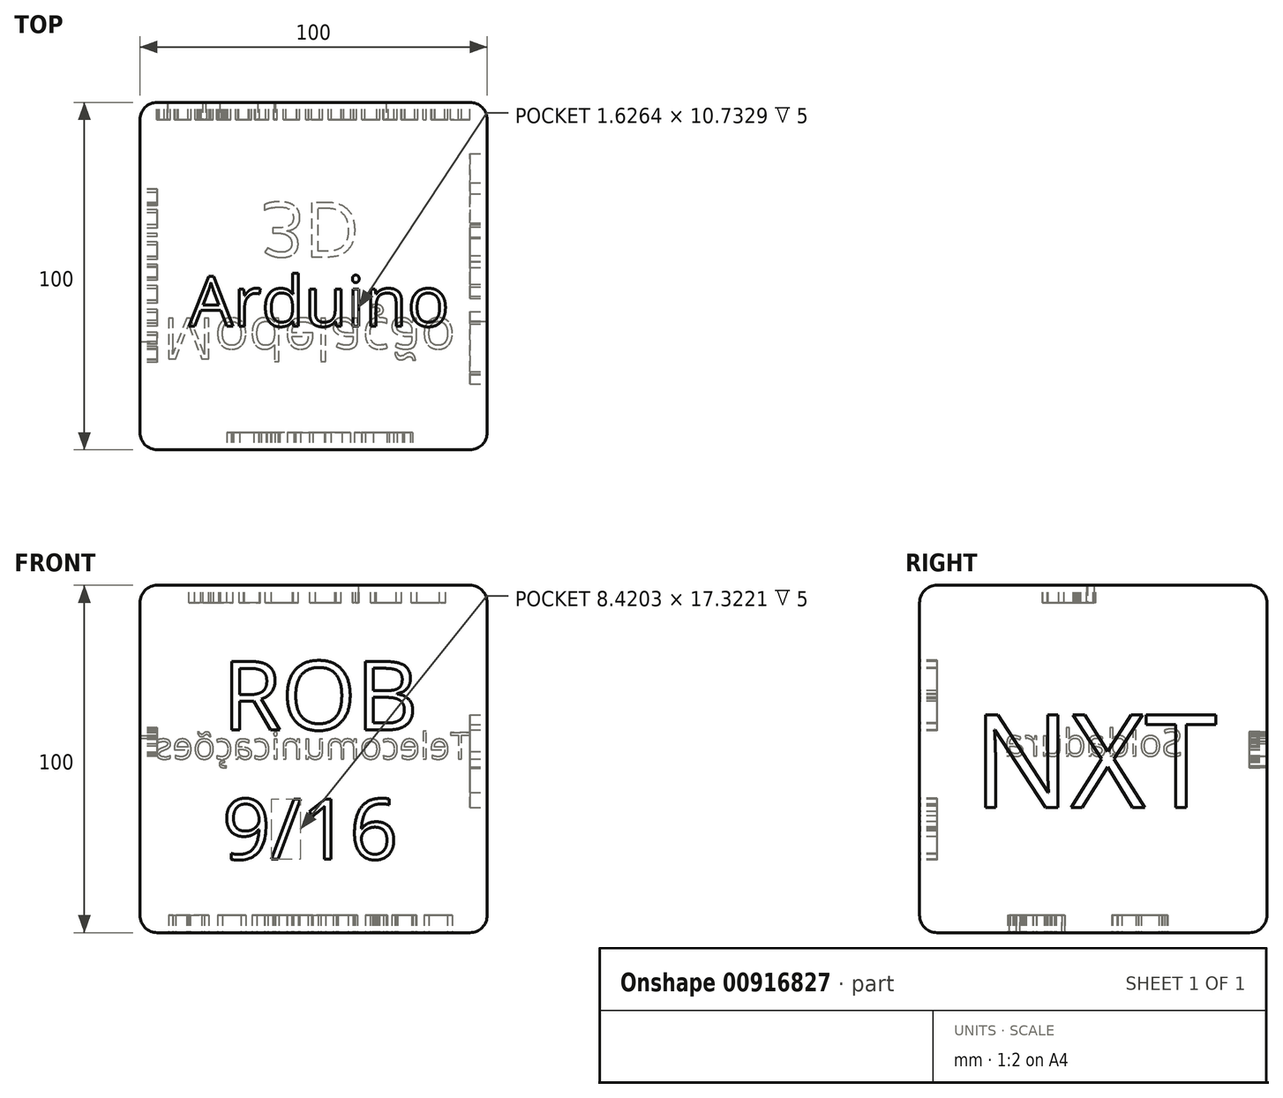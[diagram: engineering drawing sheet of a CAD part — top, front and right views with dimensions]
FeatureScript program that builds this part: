
annotation { "Feature Type Name" : "Feature", "Feature Type Description" : "" }
export const myFeature = defineFeature(function(context is Context, id is Id, definition is map)
    precondition{}
    {
        {
            var Q0;
            Q0=qCreatedBy(makeId("Top.planeOp"),FACE);
            var sketch = newSketch(context, id + "F0", { "sketchPlane" : qUnion([Q0])});
            skLineSegment(sketch, "E0.bottom", {"start": v(50, -50) * mm, "end": v(-50, -50) * mm});
            skLineSegment(sketch, "E0.top", {"start": v(50, 50) * mm, "end": v(-50, 50) * mm});
            skLineSegment(sketch, "E0.left", {"start": v(50, -50) * mm, "end": v(50, 50) * mm});
            skLineSegment(sketch, "E0.right", {"start": v(-50, -50) * mm, "end": v(-50, 50) * mm});
            skPoint(sketch, "E0.middle", {"position": v(0, 0) * mm});
            skSolve(sketch);
        }
        {
            var Q0;
            Q0=makeQuery(id+"F0.imprint","IMPRINT",FACE,{"disambiguationData":[TD([[makeQuery(id+"F0.imprint","IMPRINT",EDGE,{"derivedFrom":sQuery(id+"F0.wireOp",EDGE,"E0.bottom")}),-1.0]])]});
            extrude(context, id + "F1", {"entities" : qUnion([Q0]), "depth" : 100 * mm, "offsetDistance" : 25 * mm});
        }
        {
            var Q0;
            Q0=makeQuery(id+"F1.opExtrude","SWEPT_EDGE",EDGE,{"disambiguationData":[OSD([sQuery(id+"F0.wireOp",EDGE,"E0.bottom"),sQuery(id+"F0.wireOp",EDGE,"E0.left")])]});
            var Q1;
            Q1=makeQuery(id+"F1.opExtrude","CAP_EDGE",EDGE,{"disambiguationData":[OSD([sQuery(id+"F0.wireOp",EDGE,"E0.bottom")])],"isStart":false});
            var Q2;
            Q2=makeQuery(id+"F1.opExtrude","SWEPT_EDGE",EDGE,{"disambiguationData":[OSD([sQuery(id+"F0.wireOp",EDGE,"E0.bottom"),sQuery(id+"F0.wireOp",EDGE,"E0.right")])]});
            var Q3;
            Q3=makeQuery(id+"F1.opExtrude","CAP_EDGE",EDGE,{"disambiguationData":[OSD([sQuery(id+"F0.wireOp",EDGE,"E0.bottom")])],"isStart":true});
            var Q4;
            Q4=makeQuery(id+"F1.opExtrude","CAP_EDGE",EDGE,{"disambiguationData":[OSD([sQuery(id+"F0.wireOp",EDGE,"E0.left")])],"isStart":true});
            var Q5;
            Q5=makeQuery(id+"F1.opExtrude","CAP_EDGE",EDGE,{"disambiguationData":[OSD([sQuery(id+"F0.wireOp",EDGE,"E0.left")])],"isStart":false});
            var Q6;
            Q6=makeQuery(id+"F1.opExtrude","SWEPT_EDGE",EDGE,{"disambiguationData":[OSD([sQuery(id+"F0.wireOp",EDGE,"E0.top"),sQuery(id+"F0.wireOp",EDGE,"E0.left")])]});
            var Q7;
            Q7=makeQuery(id+"F1.opExtrude","CAP_EDGE",EDGE,{"disambiguationData":[OSD([sQuery(id+"F0.wireOp",EDGE,"E0.top")])],"isStart":false});
            var Q8;
            Q8=makeQuery(id+"F1.opExtrude","CAP_EDGE",EDGE,{"disambiguationData":[OSD([sQuery(id+"F0.wireOp",EDGE,"E0.right")])],"isStart":false});
            var Q9;
            Q9=makeQuery(id+"F1.opExtrude","CAP_EDGE",EDGE,{"disambiguationData":[OSD([sQuery(id+"F0.wireOp",EDGE,"E0.right")])],"isStart":true});
            var Q10;
            Q10=makeQuery(id+"F1.opExtrude","SWEPT_EDGE",EDGE,{"disambiguationData":[OSD([sQuery(id+"F0.wireOp",EDGE,"E0.top"),sQuery(id+"F0.wireOp",EDGE,"E0.right")])]});
            var Q11;
            Q11=makeQuery(id+"F1.opExtrude","CAP_EDGE",EDGE,{"disambiguationData":[OSD([sQuery(id+"F0.wireOp",EDGE,"E0.top")])],"isStart":true});
            fillet(context, id + "F2", {"entities" : qUnion([Q0, Q1, Q2, Q3, Q4, Q5, Q6, Q7, Q8, Q9, Q10, Q11]), "radius" : 5 * mm, "tangentPropagation" : true, "allowEdgeOverflow" : false});
        }
        {
            var Q0;
            Q0=makeQuery(id+"F1.opExtrude","SWEPT_FACE",FACE,{"disambiguationData":[OSD([sQuery(id+"F0.wireOp",EDGE,"E0.bottom")])]});
            var sketch = newSketch(context, id + "F3", { "sketchPlane" : qUnion([Q0])});
            skText(sketch, "E1", { "text": "ROB", "fontName": "OpenSans-Regular.ttf"});
            const initialGuessF3  = {"E1": [-0.02627, 0.0584, 1, 0, 0.01984]};
            skSetInitialGuess(sketch, initialGuessF3);
            skSolve(sketch);
        }
        {
            var Q0;
            Q0 = qSketchRegion(id + "F3", true);
            extrude(context, id + "F4", {"entities" : qUnion([Q0]), "operationType" : NewBodyOperationType.REMOVE, "oppositeDirection" : true, "depth" : 5 * mm, "offsetDistance" : 25 * mm});
        }
        {
            var Q0;
            {var subQ1=sQuery(id+"F0.wireOp",EDGE,"E0.bottom");Q0=makeQuery(id+"F4.boolean.opBoolean","SPLIT",FACE,{"disambiguationData":[TD([makeQuery(id+"F4.opExtrude","SWEPT_FACE",FACE,{"disambiguationData":[OSD([sQuery(id+"F3.wireOp",EDGE,"E1.sketch_text.stroke-0")])]})])],"derivedFrom":makeQuery(id+"F1.opExtrude","SWEPT_FACE",FACE,{"disambiguationData":[OSD([subQ1])]})});}
            var sketch = newSketch(context, id + "F5", { "sketchPlane" : qUnion([Q0])});
            skText(sketch, "E2", { "text": "9/16", "fontName": "OpenSans-Regular.ttf"});
            const initialGuessF5  = {"E2": [-0.02627, 0.02113, 1, 0, 0.01747]};
            skSetInitialGuess(sketch, initialGuessF5);
            skSolve(sketch);
        }
        {
            var Q0;
            Q0 = qSketchRegion(id + "F5", true);
            extrude(context, id + "F6", {"entities" : qUnion([Q0]), "operationType" : NewBodyOperationType.REMOVE, "oppositeDirection" : true, "depth" : 5 * mm, "offsetDistance" : 25 * mm});
        }
        {
            var Q0;
            Q0=makeQuery(id+"F1.opExtrude","SWEPT_FACE",FACE,{"disambiguationData":[OSD([sQuery(id+"F0.wireOp",EDGE,"E0.left")])]});
            var sketch = newSketch(context, id + "F7", { "sketchPlane" : qUnion([Q0])});
            skText(sketch, "E3", { "text": "NXT", "fontName": "OpenSans-Regular.ttf"});
            const initialGuessF7  = {"E3": [-0.03467, 0.03602, 1, 0, 0.02684]};
            skSetInitialGuess(sketch, initialGuessF7);
            skSolve(sketch);
        }
        {
            var Q0;
            Q0 = qSketchRegion(id + "F7", true);
            extrude(context, id + "F8", {"entities" : qUnion([Q0]), "operationType" : NewBodyOperationType.REMOVE, "oppositeDirection" : true, "depth" : 5 * mm, "offsetDistance" : 25 * mm});
        }
        {
            var Q0;
            Q0=makeQuery(id+"F1.opExtrude","CAP_FACE",FACE,{"disambiguationData":[OSD([sQuery(id+"F0.wireOp",EDGE,"E0.bottom"),sQuery(id+"F0.wireOp",EDGE,"E0.top"),sQuery(id+"F0.wireOp",EDGE,"E0.left"),sQuery(id+"F0.wireOp",EDGE,"E0.right")])],"isStart":false});
            var sketch = newSketch(context, id + "F9", { "sketchPlane" : qUnion([Q0])});
            skText(sketch, "E4", { "text": "Arduino", "fontName": "OpenSans-Regular.ttf"});
            const initialGuessF9  = {"E4": [-0.03588, -0.01444, 1, 0, 0.01444]};
            skSetInitialGuess(sketch, initialGuessF9);
            skSolve(sketch);
        }
        {
            var Q0;
            Q0 = qSketchRegion(id + "F9", true);
            extrude(context, id + "F10", {"entities" : qUnion([Q0]), "operationType" : NewBodyOperationType.REMOVE, "oppositeDirection" : true, "depth" : 5 * mm, "offsetDistance" : 25 * mm});
        }
        {
            var Q0;
            Q0=makeQuery(id+"F1.opExtrude","SWEPT_FACE",FACE,{"disambiguationData":[OSD([sQuery(id+"F0.wireOp",EDGE,"E0.right")])]});
            var sketch = newSketch(context, id + "F11", { "sketchPlane" : qUnion([Q0])});
            skText(sketch, "E5", { "text": "Soldadura", "fontName": "OpenSans-Regular.ttf"});
            const initialGuessF11  = {"E5": [-0.02564, 0.05084, 1, 0, 0.00776]};
            skSetInitialGuess(sketch, initialGuessF11);
            skSolve(sketch);
        }
        {
            var Q0;
            Q0 = qSketchRegion(id + "F11", true);
            extrude(context, id + "F12", {"entities" : qUnion([Q0]), "operationType" : NewBodyOperationType.REMOVE, "oppositeDirection" : true, "depth" : 5 * mm, "offsetDistance" : 25 * mm});
        }
        {
            var Q0;
            Q0=makeQuery(id+"F1.opExtrude","SWEPT_FACE",FACE,{"disambiguationData":[OSD([sQuery(id+"F0.wireOp",EDGE,"E0.top")])]});
            var sketch = newSketch(context, id + "F13", { "sketchPlane" : qUnion([Q0])});
            skText(sketch, "E6", { "text": "Telecomunicações", "fontName": "OpenSans-Regular.ttf"});
            skPoint(sketch, "E6.secondSnap0", {"position": v(-45, 50) * mm});
            const initialGuessF13  = {"E6": [-0.04513, 0.05, 1, 0, 0.00763]};
            skSetInitialGuess(sketch, initialGuessF13);
            skSolve(sketch);
        }
        {
            var Q0;
            Q0 = qSketchRegion(id + "F13", true);
            extrude(context, id + "F14", {"entities" : qUnion([Q0]), "operationType" : NewBodyOperationType.REMOVE, "oppositeDirection" : true, "depth" : 5 * mm, "offsetDistance" : 25 * mm});
        }
        {
            var Q0;
            Q0=makeQuery(id+"F1.opExtrude","CAP_FACE",FACE,{"disambiguationData":[OSD([sQuery(id+"F0.wireOp",EDGE,"E0.bottom"),sQuery(id+"F0.wireOp",EDGE,"E0.top"),sQuery(id+"F0.wireOp",EDGE,"E0.left"),sQuery(id+"F0.wireOp",EDGE,"E0.right")])],"isStart":true});
            var sketch = newSketch(context, id + "F15", { "sketchPlane" : qUnion([Q0])});
            skText(sketch, "E7", { "text": "Modelação", "fontName": "OpenSans-Regular.ttf"});
            const initialGuessF15  = {"E7": [-0.04337, 0.01211, 1, 0, 0.01183]};
            skSetInitialGuess(sketch, initialGuessF15);
            skSolve(sketch);
        }
        {
            var Q0;
            Q0 = qSketchRegion(id + "F15", true);
            extrude(context, id + "F16", {"entities" : qUnion([Q0]), "operationType" : NewBodyOperationType.REMOVE, "oppositeDirection" : true, "depth" : 5 * mm, "offsetDistance" : 25 * mm});
        }
        {
            var Q0;
            {var subQ0=sQuery(id+"F0.wireOp",EDGE,"E0.right");var subQ1=sQuery(id+"F0.wireOp",EDGE,"E0.top");var subQ2=sQuery(id+"F0.wireOp",EDGE,"E0.left");var subQ3=sQuery(id+"F0.wireOp",EDGE,"E0.bottom");Q0=makeQuery(id+"F16.boolean.opBoolean","SPLIT",FACE,{"disambiguationData":[TD([makeQuery(id+"F16.opExtrude","SWEPT_FACE",FACE,{"disambiguationData":[OSD([sQuery(id+"F15.wireOp",EDGE,"E7.sketch_text.stroke-0")])]})])],"derivedFrom":makeQuery(id+"F1.opExtrude","CAP_FACE",FACE,{"disambiguationData":[OSD([subQ3,subQ1,subQ2,subQ0])],"isStart":true})});}
            var sketch = newSketch(context, id + "F17", { "sketchPlane" : qUnion([Q0])});
            skText(sketch, "E8", { "text": "3D", "fontName": "OpenSans-Regular.ttf"});
            const initialGuessF17  = {"E8": [-0.0341, -0.02391, 1, 0, 0.01882]};
            skSetInitialGuess(sketch, initialGuessF17);
            skSolve(sketch);
        }
        {
            var Q0;
            Q0 = qSketchRegion(id + "F17", true);
            var Q1;
            Q1=makeQuery(id+"F17.imprint","IMPRINT",FACE,{"disambiguationData":[TD([[makeQuery(id+"F17.imprint","IMPRINT",EDGE,{"derivedFrom":sQuery(id+"F17.wireOp",EDGE,"E8.sketch_text.stroke-35")}),1.0]])]});
            extrude(context, id + "F18", {"entities" : qUnion([Q0, Q1]), "operationType" : NewBodyOperationType.REMOVE, "depth" : 5 * mm, "offsetDistance" : 25 * mm});
        }
        {
            var Q0;
            {var subQ0=sQuery(id+"F0.wireOp",EDGE,"E0.right");var subQ1=sQuery(id+"F0.wireOp",EDGE,"E0.top");var subQ2=sQuery(id+"F0.wireOp",EDGE,"E0.left");var subQ3=sQuery(id+"F0.wireOp",EDGE,"E0.bottom");Q0=makeQuery(id+"F16.boolean.opBoolean","SPLIT",FACE,{"disambiguationData":[TD([makeQuery(id+"F16.opExtrude","SWEPT_FACE",FACE,{"disambiguationData":[OSD([sQuery(id+"F15.wireOp",EDGE,"E7.sketch_text.stroke-0")])]})])],"derivedFrom":makeQuery(id+"F1.opExtrude","CAP_FACE",FACE,{"disambiguationData":[OSD([subQ3,subQ1,subQ2,subQ0])],"isStart":true})});}
            var sketch = newSketch(context, id + "F19", { "sketchPlane" : qUnion([Q0])});
            skText(sketch, "E9", { "text": "3D", "fontName": "OpenSans-Regular.ttf"});
            const initialGuessF19  = {"E9": [-0.01519, -0.02119, 1, 0, 0.01575]};
            skSetInitialGuess(sketch, initialGuessF19);
            skSolve(sketch);
        }
        {
            var Q0;
            Q0 = qSketchRegion(id + "F19", true);
            extrude(context, id + "F20", {"entities" : qUnion([Q0]), "operationType" : NewBodyOperationType.REMOVE, "oppositeDirection" : true, "depth" : 5 * mm, "offsetDistance" : 25 * mm});
        }
    });
